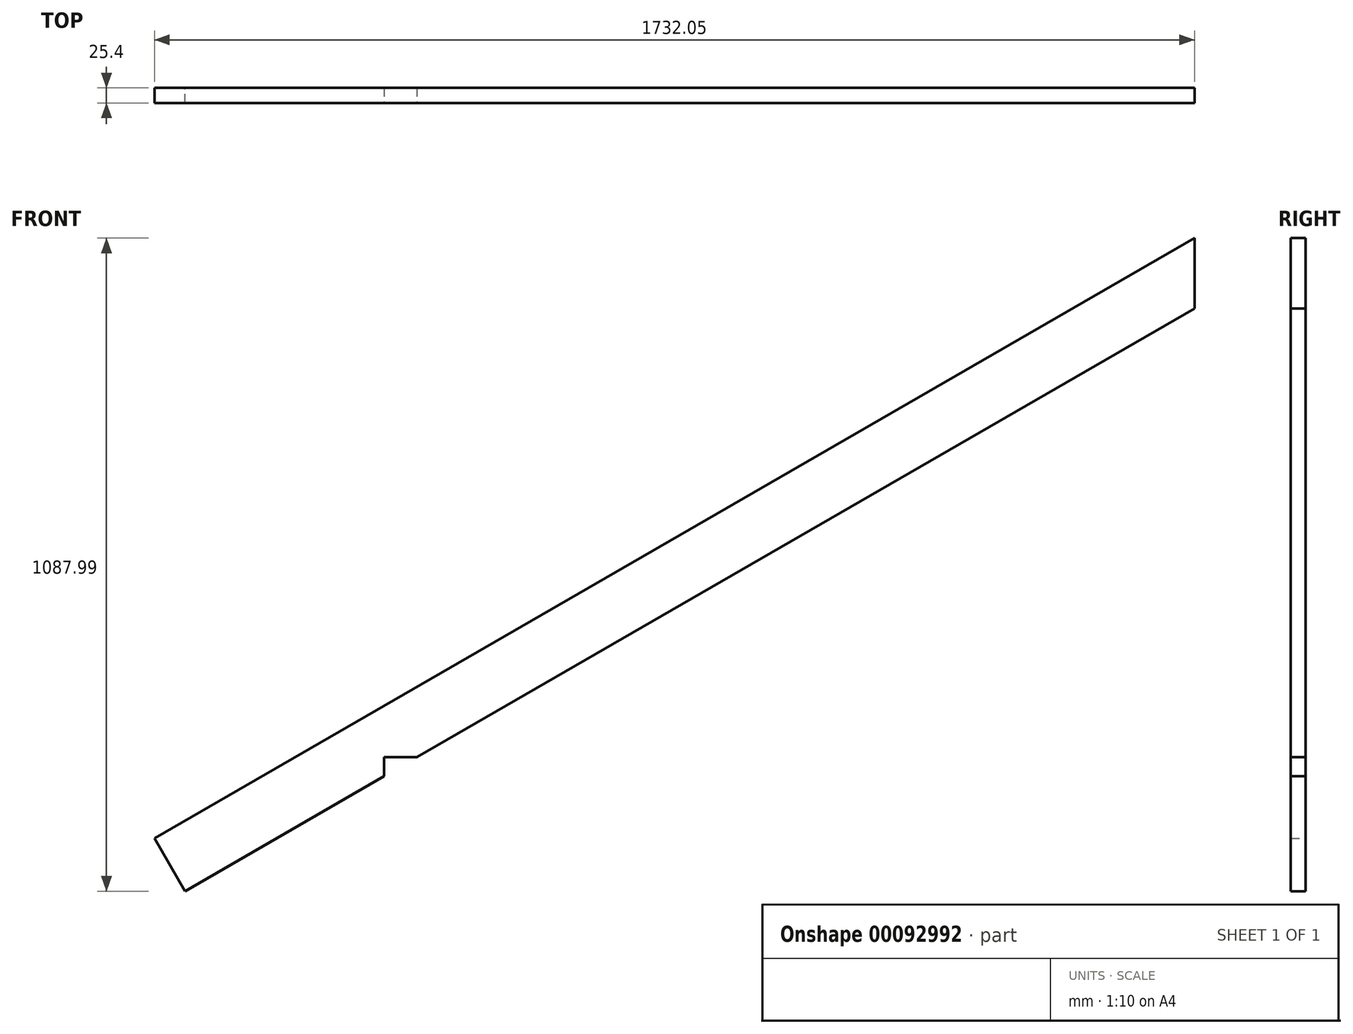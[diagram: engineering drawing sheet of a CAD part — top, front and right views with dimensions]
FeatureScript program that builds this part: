
annotation { "Feature Type Name" : "Feature", "Feature Type Description" : "" }
export const myFeature = defineFeature(function(context is Context, id is Id, definition is map)
    precondition{}
    {
        {
            var Q0;
            Q0=qCreatedBy(makeId("Front.planeOp"),FACE);
            var sketch = newSketch(context, id + "F0", { "sketchPlane" : qUnion([Q0])});
            skLineSegment(sketch, "E0", {"start": v(-1250, 0) * mm, "end": v(1250, 0) * mm, "construction": true});
            skLineSegment(sketch, "E1", {"start": v(-1250, 0) * mm, "end": v(0, 721.69) * mm, "construction": true});
            skLineSegment(sketch, "E2", {"start": v(0, 721.69) * mm, "end": v(1250, 0) * mm, "construction": true});
            skLineSegment(sketch, "E3", {"start": v(-1732.05, -278.31) * mm, "end": v(-1681.25, -366.3) * mm});
            skLineSegment(sketch, "E4", {"start": v(-1681.25, -366.3) * mm, "end": v(0, 604.37) * mm});
            skLineSegment(sketch, "E5", {"start": v(-1732.05, -278.31) * mm, "end": v(0, 721.69) * mm});
            skLineSegment(sketch, "E6", {"start": v(0, 721.69) * mm, "end": v(0, 604.37) * mm});
            skSolve(sketch);
        }
        {
            var Q0;
            Q0=makeQuery(id+"F0.imprint","IMPRINT",FACE,{"disambiguationData":[TD([[makeQuery(id+"F0.imprint","IMPRINT",EDGE,{"derivedFrom":sQuery(id+"F0.wireOp",EDGE,"E3")}),1.0]])]});
            extrude(context, id + "F1", {"entities" : qUnion([Q0]), "endBound" : BoundingType.SYMMETRIC, "depth" : 25.4 * mm});
        }
        {
            var Q0;
            Q0=qCreatedBy(makeId("Front.planeOp"),FACE);
            var sketch = newSketch(context, id + "F2", { "sketchPlane" : qUnion([Q0])});
            skLineSegment(sketch, "E7.bottom", {"start": v(-1350, -143.31) * mm, "end": v(-1248.4, -143.31) * mm});
            skLineSegment(sketch, "E7.top", {"start": v(-1350, -244.91) * mm, "end": v(-1248.4, -244.91) * mm});
            skLineSegment(sketch, "E7.left", {"start": v(-1350, -143.31) * mm, "end": v(-1350, -244.91) * mm});
            skLineSegment(sketch, "E7.right", {"start": v(-1248.4, -143.31) * mm, "end": v(-1248.4, -244.91) * mm});
            skLineSegment(sketch, "E8.0", {"start": v(-1681.25, -366.3) * mm, "end": v(0, 604.37) * mm, "construction": true});
            skLineSegment(sketch, "E9", {"start": v(-1746.46, -244.91) * mm, "end": v(0, -244.91) * mm, "construction": true});
            skSolve(sketch);
        }
        {
            var Q0;
            Q0 = qSketchRegion(id + "F2", true);
            extrude(context, id + "F3", {"entities" : qUnion([Q0]), "operationType" : NewBodyOperationType.REMOVE, "endBound" : BoundingType.SYMMETRIC, "oppositeDirection" : true, "depth" : 50 * mm});
        }
    });
